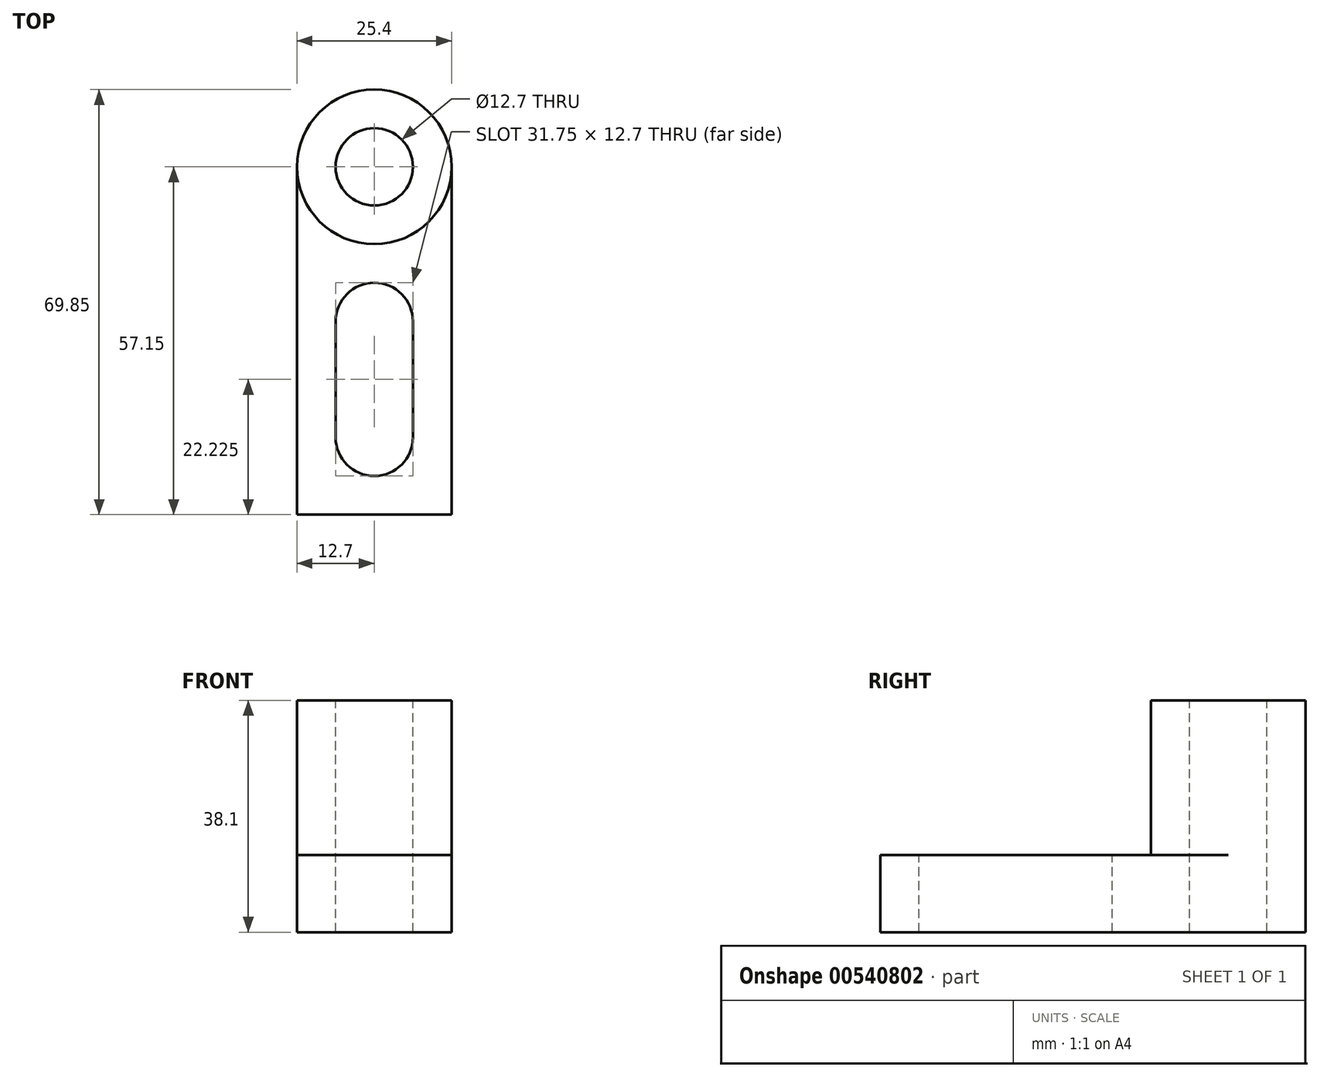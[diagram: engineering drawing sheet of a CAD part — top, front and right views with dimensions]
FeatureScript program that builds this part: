
annotation { "Feature Type Name" : "Feature", "Feature Type Description" : "" }
export const myFeature = defineFeature(function(context is Context, id is Id, definition is map)
    precondition{}
    {
        {
            var Q0;
            Q0=qCreatedBy(makeId("Top.planeOp"),FACE);
            var sketch = newSketch(context, id + "F0", { "sketchPlane" : qUnion([Q0])});
            skLineSegment(sketch, "E0", {"start": v(0, 0) * mm, "end": v(0, 69.85) * mm});
            skLineSegment(sketch, "E1", {"start": v(0, 69.85) * mm, "end": v(25.4, 69.85) * mm});
            skLineSegment(sketch, "E2", {"start": v(25.4, 69.85) * mm, "end": v(25.4, 0) * mm});
            skLineSegment(sketch, "E3", {"start": v(25.4, 0) * mm, "end": v(0, 0) * mm});
            skSolve(sketch);
        }
        {
            var Q0;
            Q0 = qSketchRegion(id + "F0", true);
            extrude(context, id + "F1", {"entities" : qUnion([Q0]), "depth" : 38.1 * mm, "offsetDistance" : 25.4 * mm});
        }
        {
            var Q0;
            Q0=makeQuery(id+"F1.opExtrude","SWEPT_FACE",FACE,{"disambiguationData":[OSD([sQuery(id+"F0.wireOp",EDGE,"E0")])]});
            var sketch = newSketch(context, id + "F2", { "sketchPlane" : qUnion([Q0])});
            skLineSegment(sketch, "E4", {"start": v(-44.45, 38.1) * mm, "end": v(-44.45, 12.7) * mm});
            skLineSegment(sketch, "E5", {"start": v(-44.45, 12.7) * mm, "end": v(0, 12.7) * mm});
            skLineSegment(sketch, "E6", {"start": v(0, 12.7) * mm, "end": v(0, 38.1) * mm});
            skLineSegment(sketch, "E7", {"start": v(0, 38.1) * mm, "end": v(-44.45, 38.1) * mm});
            skSolve(sketch);
        }
        {
            var Q0;
            Q0=makeQuery(id+"F2.imprint","IMPRINT",FACE,{"disambiguationData":[TD([[makeQuery(id+"F2.imprint","IMPRINT",EDGE,{"derivedFrom":sQuery(id+"F2.wireOp",EDGE,"E4")}),1.0]])]});
            extrude(context, id + "F3", {"entities" : qUnion([Q0]), "operationType" : NewBodyOperationType.REMOVE, "oppositeDirection" : true, "depth" : 25.4 * mm, "offsetDistance" : 25.4 * mm});
        }
        {
            var Q0;
            Q0=makeQuery(id+"F1.opExtrude","CAP_FACE",FACE,{"disambiguationData":[OSD([sQuery(id+"F0.wireOp",EDGE,"E0"),sQuery(id+"F0.wireOp",EDGE,"E1"),sQuery(id+"F0.wireOp",EDGE,"E2"),sQuery(id+"F0.wireOp",EDGE,"E3")])],"isStart":false});
            var sketch = newSketch(context, id + "F4", { "sketchPlane" : qUnion([Q0])});
            skSolve(sketch);
        }
        {
            var Q0;
            Q0 = qSketchRegion(id + "F2", true);
            extrude(context, id + "F5", {"entities" : qUnion([Q0]), "operationType" : NewBodyOperationType.REMOVE, "oppositeDirection" : true, "depth" : 25.4 * mm, "offsetDistance" : 25.4 * mm});
        }
        {
            var Q0;
            Q0=makeQuery(id+"F4.imprint","IMPRINT",FACE,{"disambiguationData":[TD([[makeQuery(id+"F4.imprint","IMPRINT",EDGE,{"derivedFrom":makeQuery(id+"F1.opExtrude","CAP_EDGE",EDGE,{"disambiguationData":[OSD([sQuery(id+"F0.wireOp",EDGE,"E1")])],"isStart":false})}),-1.0]])]});
            var sketch = newSketch(context, id + "F6", { "sketchPlane" : qUnion([Q0])});
            skCircle(sketch, "E8", {"center": v(12.7, 57.15) * mm, "radius": 12.7 * mm});
            skSolve(sketch);
        }
        {
            var Q0;
            {var subQ0=sQuery(id+"F6.wireOp",EDGE,"E8");var subQ1=makeQuery(id+"F4.imprint","IMPRINT",EDGE,{"derivedFrom":makeQuery(id+"F1.opExtrude","CAP_EDGE",EDGE,{"disambiguationData":[OSD([sQuery(id+"F0.wireOp",EDGE,"E1")])],"isStart":false})});var subQ2=makeQuery(id+"F6.imprint","INTERSECT",VERTEX,{"derivedFrom":[subQ1,subQ0]});Q0=makeQuery(id+"F6.imprint","IMPRINT",FACE,{"disambiguationData":[TD([[makeQuery(id+"F6.imprint","IMPRINT",EDGE,{"disambiguationData":[TD([[subQ2,-1.0]])],"derivedFrom":subQ0}),-1.0]])]});}
            var Q1;
            {var subQ0=sQuery(id+"F6.wireOp",EDGE,"E8");var subQ1=makeQuery(id+"F4.imprint","IMPRINT",EDGE,{"derivedFrom":makeQuery(id+"F1.opExtrude","CAP_EDGE",EDGE,{"disambiguationData":[OSD([sQuery(id+"F0.wireOp",EDGE,"E1")])],"isStart":false})});var subQ2=makeQuery(id+"F6.imprint","INTERSECT",VERTEX,{"derivedFrom":[subQ1,subQ0]});Q1=makeQuery(id+"F6.imprint","IMPRINT",FACE,{"disambiguationData":[TD([[makeQuery(id+"F6.imprint","IMPRINT",EDGE,{"disambiguationData":[TD([[subQ2,1.0]])],"derivedFrom":subQ0}),-1.0]])]});}
            var Q2;
            {var subQ0=sQuery(id+"F6.wireOp",EDGE,"E8");var subQ1=sQuery(id+"F0.wireOp",EDGE,"E0");var subQ2=makeQuery(id+"F4.imprint","IMPRINT",EDGE,{"derivedFrom":makeQuery(id+"F1.opExtrude","CAP_EDGE",EDGE,{"disambiguationData":[OSD([subQ1])],"isStart":false})});var subQ3=makeQuery(id+"F6.imprint","INTERSECT",VERTEX,{"derivedFrom":[subQ2,subQ0]});Q2=makeQuery(id+"F6.imprint","IMPRINT",FACE,{"disambiguationData":[TD([[makeQuery(id+"F6.imprint","IMPRINT",EDGE,{"disambiguationData":[TD([[subQ3,-1.0]])],"derivedFrom":subQ0}),-1.0]])]});}
            var Q3;
            {var subQ0=sQuery(id+"F6.wireOp",EDGE,"E8");var subQ1=makeQuery(id+"F4.imprint","IMPRINT",EDGE,{"derivedFrom":makeQuery(id+"F1.opExtrude","CAP_EDGE",EDGE,{"disambiguationData":[OSD([sQuery(id+"F0.wireOp",EDGE,"E2")])],"isStart":false})});var subQ2=makeQuery(id+"F6.imprint","INTERSECT",VERTEX,{"derivedFrom":[subQ1,subQ0]});Q3=makeQuery(id+"F6.imprint","IMPRINT",FACE,{"disambiguationData":[TD([[makeQuery(id+"F6.imprint","IMPRINT",EDGE,{"disambiguationData":[TD([[subQ2,1.0]])],"derivedFrom":subQ0}),-1.0]])]});}
            extrude(context, id + "F7", {"entities" : qUnion([Q0, Q1, Q2, Q3]), "operationType" : NewBodyOperationType.REMOVE, "oppositeDirection" : true, "depth" : 25.4 * mm, "offsetDistance" : 25.4 * mm});
        }
        {
            var Q0;
            Q0=makeQuery(id+"F4.imprint","IMPRINT",FACE,{"disambiguationData":[TD([[makeQuery(id+"F4.imprint","IMPRINT",EDGE,{"derivedFrom":makeQuery(id+"F1.opExtrude","CAP_EDGE",EDGE,{"disambiguationData":[OSD([sQuery(id+"F0.wireOp",EDGE,"E1")])],"isStart":false})}),-1.0]])]});
            extrude(context, id + "F8", {"entities" : qUnion([Q0]), "operationType" : NewBodyOperationType.REMOVE, "depth" : 25.4 * mm, "offsetDistance" : 25.4 * mm});
        }
        {
            var Q0;
            Q0=makeQuery(id+"F1.opExtrude","CAP_FACE",FACE,{"disambiguationData":[OSD([sQuery(id+"F0.wireOp",EDGE,"E0"),sQuery(id+"F0.wireOp",EDGE,"E1"),sQuery(id+"F0.wireOp",EDGE,"E2"),sQuery(id+"F0.wireOp",EDGE,"E3")])],"isStart":false});
            var sketch = newSketch(context, id + "F9", { "sketchPlane" : qUnion([Q0])});
            skCircle(sketch, "E9", {"center": v(12.7, 57.15) * mm, "radius": 6.35 * mm});
            skSolve(sketch);
        }
        {
            var Q0;
            Q0=makeQuery(id+"F9.imprint","IMPRINT",FACE,{"disambiguationData":[TD([[makeQuery(id+"F9.imprint","IMPRINT",EDGE,{"derivedFrom":sQuery(id+"F9.wireOp",EDGE,"E9")}),1.0]])]});
            extrude(context, id + "F10", {"entities" : qUnion([Q0]), "operationType" : NewBodyOperationType.REMOVE, "oppositeDirection" : true, "depth" : 76.2 * mm, "offsetDistance" : 25.4 * mm});
        }
        {
            var Q0;
            Q0=makeQuery(id+"F7.boolean.opBoolean","COPY",FACE,{"derivedFrom":makeQuery(id+"F7.opExtrude","CAP_FACE",FACE,{"disambiguationData":[OSD([sQuery(id+"F0.wireOp",EDGE,"E0"),sQuery(id+"F0.wireOp",EDGE,"E1"),sQuery(id+"F6.wireOp",EDGE,"E8")])],"isStart":false})});
            var Q1;
            Q1=makeQuery(id+"F7.boolean.opBoolean","COPY",FACE,{"derivedFrom":makeQuery(id+"F7.opExtrude","CAP_FACE",FACE,{"disambiguationData":[OSD([sQuery(id+"F0.wireOp",EDGE,"E1"),sQuery(id+"F0.wireOp",EDGE,"E2"),sQuery(id+"F6.wireOp",EDGE,"E8")])],"isStart":false})});
            extrude(context, id + "F11", {"entities" : qUnion([Q0, Q1]), "operationType" : NewBodyOperationType.REMOVE, "oppositeDirection" : true, "depth" : 25.4 * mm, "offsetDistance" : 25.4 * mm});
        }
        {
            var Q0;
            {var subQ0=sQuery(id+"F6.wireOp",EDGE,"E8");var subQ1=sQuery(id+"F2.wireOp",EDGE,"E7");var subQ2=sQuery(id+"F2.wireOp",EDGE,"E4");var subQ3=sQuery(id+"F0.wireOp",EDGE,"E0");Q0=makeQuery(id+"F7.boolean.opBoolean","MERGE",FACE,{"derivedFrom":[makeQuery(id+"F3.boolean.opBoolean","COPY",FACE,{"derivedFrom":makeQuery(id+"F3.opExtrude","SWEPT_FACE",FACE,{"disambiguationData":[OSD([sQuery(id+"F2.wireOp",EDGE,"E5")])]})})],"fromTools":[makeQuery(id+"F7.opExtrude","CAP_FACE",FACE,{"disambiguationData":[OSD([subQ3,subQ2,subQ1,subQ0])],"isStart":false}),makeQuery(id+"F7.opExtrude","CAP_FACE",FACE,{"disambiguationData":[OSD([subQ3,sQuery(id+"F0.wireOp",EDGE,"E2"),subQ2,subQ1,subQ0])],"isStart":false})]});}
            var sketch = newSketch(context, id + "F12", { "sketchPlane" : qUnion([Q0])});
            skCircle(sketch, "E10", {"center": v(12.7, 31.75) * mm, "radius": 6.35 * mm});
            skCircle(sketch, "E11", {"center": v(12.7, 12.7) * mm, "radius": 6.35 * mm});
            skLineSegment(sketch, "E12", {"start": v(19.05, 12.7) * mm, "end": v(19.05, 31.75) * mm});
            skLineSegment(sketch, "E13", {"start": v(19.05, 31.75) * mm, "end": v(6.35, 31.75) * mm});
            skLineSegment(sketch, "E14", {"start": v(6.35, 31.75) * mm, "end": v(6.35, 12.7) * mm});
            skSolve(sketch);
        }
        {
            var Q0;
            Q0 = qSketchRegion(id + "F12", true);
            extrude(context, id + "F13", {"entities" : qUnion([Q0]), "operationType" : NewBodyOperationType.REMOVE, "oppositeDirection" : true, "depth" : 25.4 * mm, "offsetDistance" : 25.4 * mm});
        }
    });
